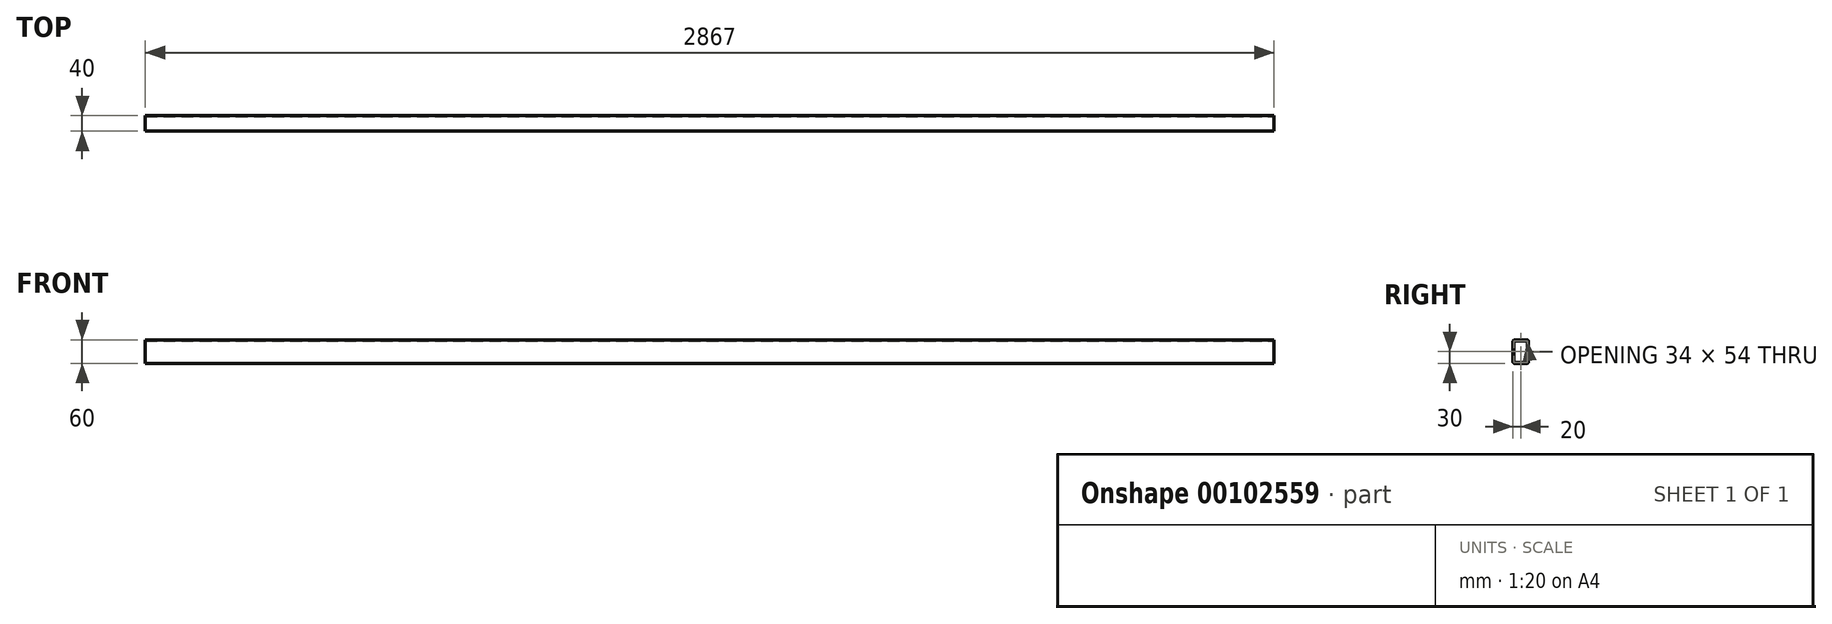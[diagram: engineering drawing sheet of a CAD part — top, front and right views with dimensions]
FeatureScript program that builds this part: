
annotation { "Feature Type Name" : "Feature", "Feature Type Description" : "" }
export const myFeature = defineFeature(function(context is Context, id is Id, definition is map)
    precondition{}
    {
        {
            var Q0;
            Q0=qCreatedBy(makeId("Front.planeOp"),FACE);
            var sketch = newSketch(context, id + "F0", { "sketchPlane" : qUnion([Q0])});
            skLineSegment(sketch, "E0.bottom", {"start": v(0, 0) * mm, "end": v(2867, 0) * mm});
            skLineSegment(sketch, "E0.top", {"start": v(0, 60) * mm, "end": v(2867, 60) * mm});
            skLineSegment(sketch, "E0.left", {"start": v(0, 0) * mm, "end": v(0, 60) * mm});
            skLineSegment(sketch, "E0.right", {"start": v(2867, 0) * mm, "end": v(2867, 60) * mm});
            skSolve(sketch);
        }
        {
            var Q0;
            Q0 = qSketchRegion(id + "F0", true);
            extrude(context, id + "F1", {"entities" : qUnion([Q0]), "depth" : 40 * mm, "offsetDistance" : 25 * mm});
        }
        {
            var Q0;
            Q0=makeQuery(id+"F1.opExtrude","SWEPT_FACE",FACE,{"disambiguationData":[OSD([sQuery(id+"F0.wireOp",EDGE,"E0.left")])]});
            var Q1;
            Q1=makeQuery(id+"F1.opExtrude","SWEPT_FACE",FACE,{"disambiguationData":[OSD([sQuery(id+"F0.wireOp",EDGE,"E0.right")])]});
            shell(context, id + "F2", {"entities" : qUnion([Q0, Q1]), "thickness" : 3 * mm});
        }
        {
            var Q0;
            Q0=makeQuery(id+"F1.opExtrude","CAP_EDGE",EDGE,{"disambiguationData":[OSD([sQuery(id+"F0.wireOp",EDGE,"E0.top")])],"isStart":false});
            var Q1;
            Q1=makeQuery(id+"F1.opExtrude","CAP_EDGE",EDGE,{"disambiguationData":[OSD([sQuery(id+"F0.wireOp",EDGE,"E0.bottom")])],"isStart":false});
            var Q2;
            Q2=makeQuery(id+"F1.opExtrude","CAP_EDGE",EDGE,{"disambiguationData":[OSD([sQuery(id+"F0.wireOp",EDGE,"E0.bottom")])],"isStart":true});
            var Q3;
            Q3=makeQuery(id+"F1.opExtrude","CAP_EDGE",EDGE,{"disambiguationData":[OSD([sQuery(id+"F0.wireOp",EDGE,"E0.top")])],"isStart":true});
            fillet(context, id + "F3", {"entities" : qUnion([Q0, Q1, Q2, Q3]), "tangentPropagation" : true, "radius" : 5 * mm, "defaultsChanged" : false, "vertexSettings" : [], "allowEdgeOverflow" : false});
        }
        {
            var Q0;
            {var subQ0=sQuery(id+"F0.wireOp",EDGE,"E0.bottom");Q0=makeQuery(id+"F2.opShell","OFFSET_EDGE",EDGE,{"disambiguationData":[OSD([subQ0]),TDD([makeQuery(id+"F1.opExtrude","CAP_EDGE",EDGE,{"disambiguationData":[OSD([subQ0])],"isStart":true})])]});}
            var Q1;
            {var subQ0=sQuery(id+"F0.wireOp",EDGE,"E0.bottom");Q1=makeQuery(id+"F2.opShell","OFFSET_EDGE",EDGE,{"disambiguationData":[OSD([subQ0]),TDD([makeQuery(id+"F1.opExtrude","CAP_EDGE",EDGE,{"disambiguationData":[OSD([subQ0])],"isStart":false})])]});}
            var Q2;
            {var subQ0=sQuery(id+"F0.wireOp",EDGE,"E0.top");Q2=makeQuery(id+"F2.opShell","OFFSET_EDGE",EDGE,{"disambiguationData":[OSD([subQ0]),TDD([makeQuery(id+"F1.opExtrude","CAP_EDGE",EDGE,{"disambiguationData":[OSD([subQ0])],"isStart":true})])]});}
            var Q3;
            {var subQ0=sQuery(id+"F0.wireOp",EDGE,"E0.top");Q3=makeQuery(id+"F2.opShell","OFFSET_EDGE",EDGE,{"disambiguationData":[OSD([subQ0]),TDD([makeQuery(id+"F1.opExtrude","CAP_EDGE",EDGE,{"disambiguationData":[OSD([subQ0])],"isStart":false})])]});}
            fillet(context, id + "F4", {"entities" : qUnion([Q0, Q1, Q2, Q3]), "tangentPropagation" : true, "radius" : 1 * mm, "defaultsChanged" : false, "vertexSettings" : [], "allowEdgeOverflow" : false});
        }
    });
